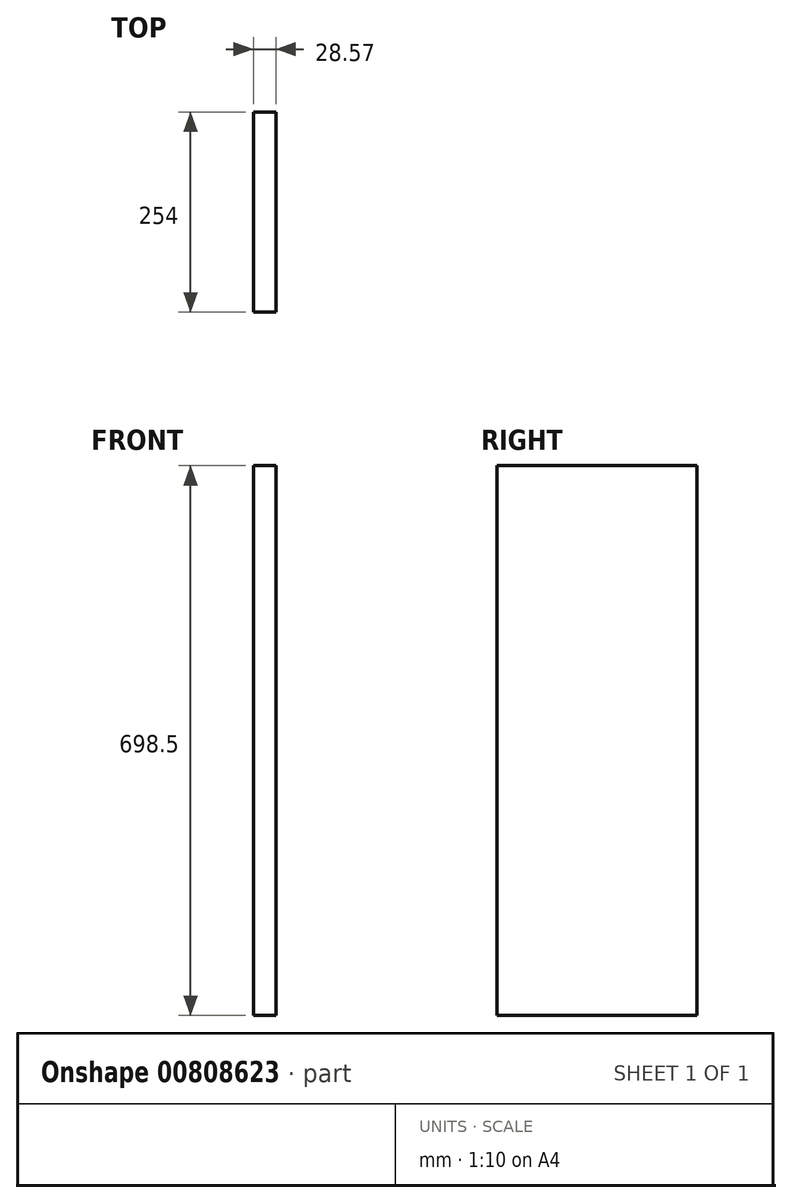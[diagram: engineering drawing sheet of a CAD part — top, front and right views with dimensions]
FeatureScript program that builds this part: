
annotation { "Feature Type Name" : "Feature", "Feature Type Description" : "" }
export const myFeature = defineFeature(function(context is Context, id is Id, definition is map)
    precondition{}
    {
        {
            var Q0;
            Q0=qCreatedBy(makeId("Right.planeOp"),FACE);
            var sketch = newSketch(context, id + "F0", { "sketchPlane" : qUnion([Q0])});
            skLineSegment(sketch, "E0.bottom", {"start": v(127, 349.25) * mm, "end": v(-127, 349.25) * mm});
            skLineSegment(sketch, "E0.top", {"start": v(127, -349.25) * mm, "end": v(-127, -349.25) * mm});
            skLineSegment(sketch, "E0.left", {"start": v(127, 349.25) * mm, "end": v(127, -349.25) * mm});
            skLineSegment(sketch, "E0.right", {"start": v(-127, 349.25) * mm, "end": v(-127, -349.25) * mm});
            skPoint(sketch, "E0.middle", {"position": v(0, 0) * mm});
            skSolve(sketch);
        }
        {
            var Q0;
            Q0=makeQuery(id+"F0.imprint","IMPRINT",FACE,{"disambiguationData":[TD([[makeQuery(id+"F0.imprint","IMPRINT",EDGE,{"derivedFrom":sQuery(id+"F0.wireOp",EDGE,"E0.bottom")}),1.0]])]});
            extrude(context, id + "F1", {"entities" : qUnion([Q0]), "depth" : 28.57 * mm, "offsetDistance" : 25.4 * mm});
        }
    });
